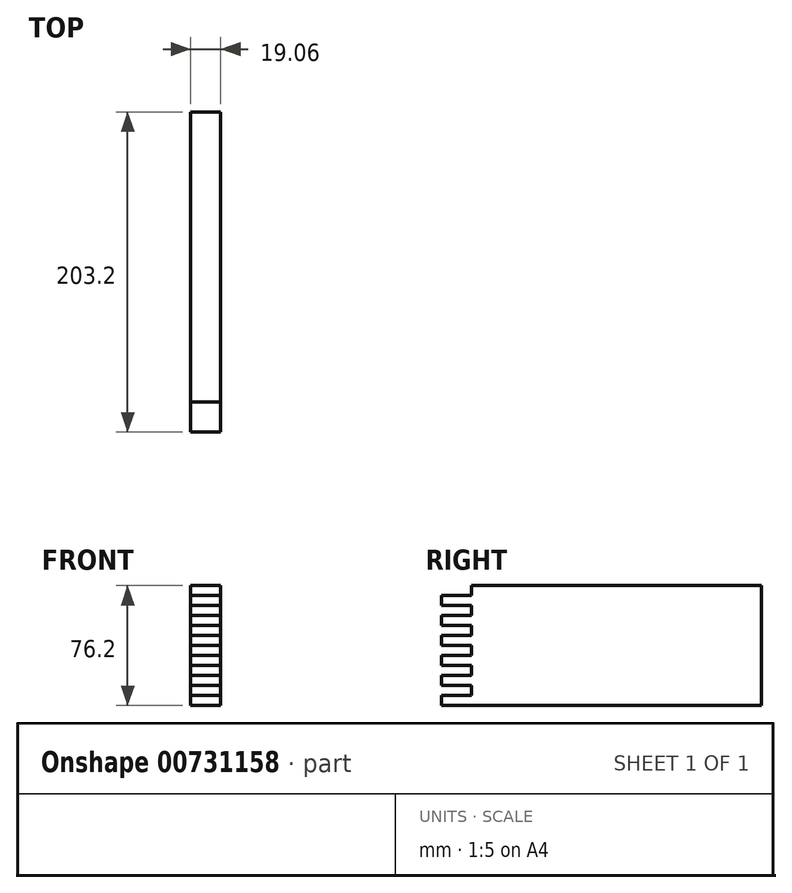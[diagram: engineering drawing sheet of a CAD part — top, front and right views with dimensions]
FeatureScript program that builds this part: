
annotation { "Feature Type Name" : "Feature", "Feature Type Description" : "" }
export const myFeature = defineFeature(function(context is Context, id is Id, definition is map)
    precondition{}
    {
        {
            var Q0;
            Q0=qCreatedBy(makeId("Front.planeOp"),FACE);
            var sketch = newSketch(context, id + "F0", { "sketchPlane" : qUnion([Q0])});
            skLineSegment(sketch, "E0.bottom", {"start": v(9.52, -38.1) * mm, "end": v(-9.53, -38.1) * mm});
            skLineSegment(sketch, "E0.top", {"start": v(9.53, 38.1) * mm, "end": v(-9.52, 38.1) * mm});
            skLineSegment(sketch, "E0.left", {"start": v(9.52, -38.1) * mm, "end": v(9.53, 38.1) * mm});
            skLineSegment(sketch, "E0.right", {"start": v(-9.53, -38.1) * mm, "end": v(-9.52, 38.1) * mm});
            skPoint(sketch, "E0.middle", {"position": v(0, 0) * mm});
            skSolve(sketch);
        }
        {
            var Q0;
            Q0 = qSketchRegion(id + "F0", true);
            extrude(context, id + "F1", {"entities" : qUnion([Q0]), "endBound" : BoundingType.SYMMETRIC, "depth" : 203.2 * mm, "offsetDistance" : 25.4 * mm});
        }
        {
            var Q0;
            Q0=makeQuery(id+"F1.opExtrude","SWEPT_FACE",FACE,{"disambiguationData":[OSD([sQuery(id+"F0.wireOp",EDGE,"E0.left")])]});
            var sketch = newSketch(context, id + "F2", { "sketchPlane" : qUnion([Q0])});
            skLineSegment(sketch, "E1", {"start": v(-82.55, 38.1) * mm, "end": v(-82.55, -38.1) * mm});
            skLineSegment(sketch, "E2", {"start": v(-101.6, 31.75) * mm, "end": v(-82.55, 31.75) * mm});
            skLineSegment(sketch, "E3", {"start": v(-101.6, 25.4) * mm, "end": v(-82.55, 25.4) * mm});
            skLineSegment(sketch, "E4", {"start": v(-101.6, 19.05) * mm, "end": v(-82.55, 19.05) * mm});
            skLineSegment(sketch, "E5", {"start": v(-101.6, 12.7) * mm, "end": v(-82.55, 12.7) * mm});
            skPoint(sketch, "E5.endSnap0", {"position": v(-82.55, 0) * mm});
            skLineSegment(sketch, "E6", {"start": v(-101.6, -12.7) * mm, "end": v(-82.55, -12.7) * mm});
            skLineSegment(sketch, "E7", {"start": v(-101.6, -19.05) * mm, "end": v(-82.55, -19.05) * mm});
            skLineSegment(sketch, "E8", {"start": v(-101.6, -25.4) * mm, "end": v(-82.55, -25.4) * mm});
            skLineSegment(sketch, "E9", {"start": v(-82.55, 6.35) * mm, "end": v(-101.6, 6.35) * mm});
            skLineSegment(sketch, "E10", {"start": v(-101.6, 0) * mm, "end": v(-82.55, 0) * mm});
            skLineSegment(sketch, "E11", {"start": v(-101.6, -6.35) * mm, "end": v(-82.55, -6.35) * mm});
            skLineSegment(sketch, "E12", {"start": v(-101.6, -31.75) * mm, "end": v(-82.55, -31.75) * mm});
            skSolve(sketch);
        }
        {
            var Q0;
            {var subQ4=sQuery(id+"F2.wireOp",EDGE,"E2");Q0=makeQuery(id+"F2.imprint","IMPRINT",FACE,{"disambiguationData":[TD([[makeQuery(id+"F2.imprint","IMPRINT",EDGE,{"derivedFrom":subQ4}),1.0]])]});}
            var Q1;
            {var subQ0=sQuery(id+"F2.wireOp",EDGE,"E3");Q1=makeQuery(id+"F2.imprint","IMPRINT",FACE,{"disambiguationData":[TD([[makeQuery(id+"F2.imprint","IMPRINT",EDGE,{"derivedFrom":subQ0}),-1.0]])]});}
            var Q2;
            {var subQ0=sQuery(id+"F2.wireOp",EDGE,"E5");Q2=makeQuery(id+"F2.imprint","IMPRINT",FACE,{"disambiguationData":[TD([[makeQuery(id+"F2.imprint","IMPRINT",EDGE,{"derivedFrom":subQ0}),-1.0]])]});}
            var Q3;
            {var subQ0=sQuery(id+"F2.wireOp",EDGE,"E10");Q3=makeQuery(id+"F2.imprint","IMPRINT",FACE,{"disambiguationData":[TD([[makeQuery(id+"F2.imprint","IMPRINT",EDGE,{"derivedFrom":subQ0}),-1.0]])]});}
            var Q4;
            {var subQ0=sQuery(id+"F2.wireOp",EDGE,"E6");Q4=makeQuery(id+"F2.imprint","IMPRINT",FACE,{"disambiguationData":[TD([[makeQuery(id+"F2.imprint","IMPRINT",EDGE,{"derivedFrom":subQ0}),-1.0]])]});}
            var Q5;
            {var subQ0=sQuery(id+"F2.wireOp",EDGE,"E8");Q5=makeQuery(id+"F2.imprint","IMPRINT",FACE,{"disambiguationData":[TD([[makeQuery(id+"F2.imprint","IMPRINT",EDGE,{"derivedFrom":subQ0}),-1.0]])]});}
            extrude(context, id + "F3", {"entities" : qUnion([Q0, Q1, Q2, Q3, Q4, Q5]), "operationType" : NewBodyOperationType.REMOVE, "endBound" : BoundingType.THROUGH_ALL, "oppositeDirection" : true, "depth" : 25.4 * mm, "offsetDistance" : 25.4 * mm});
        }
    });
